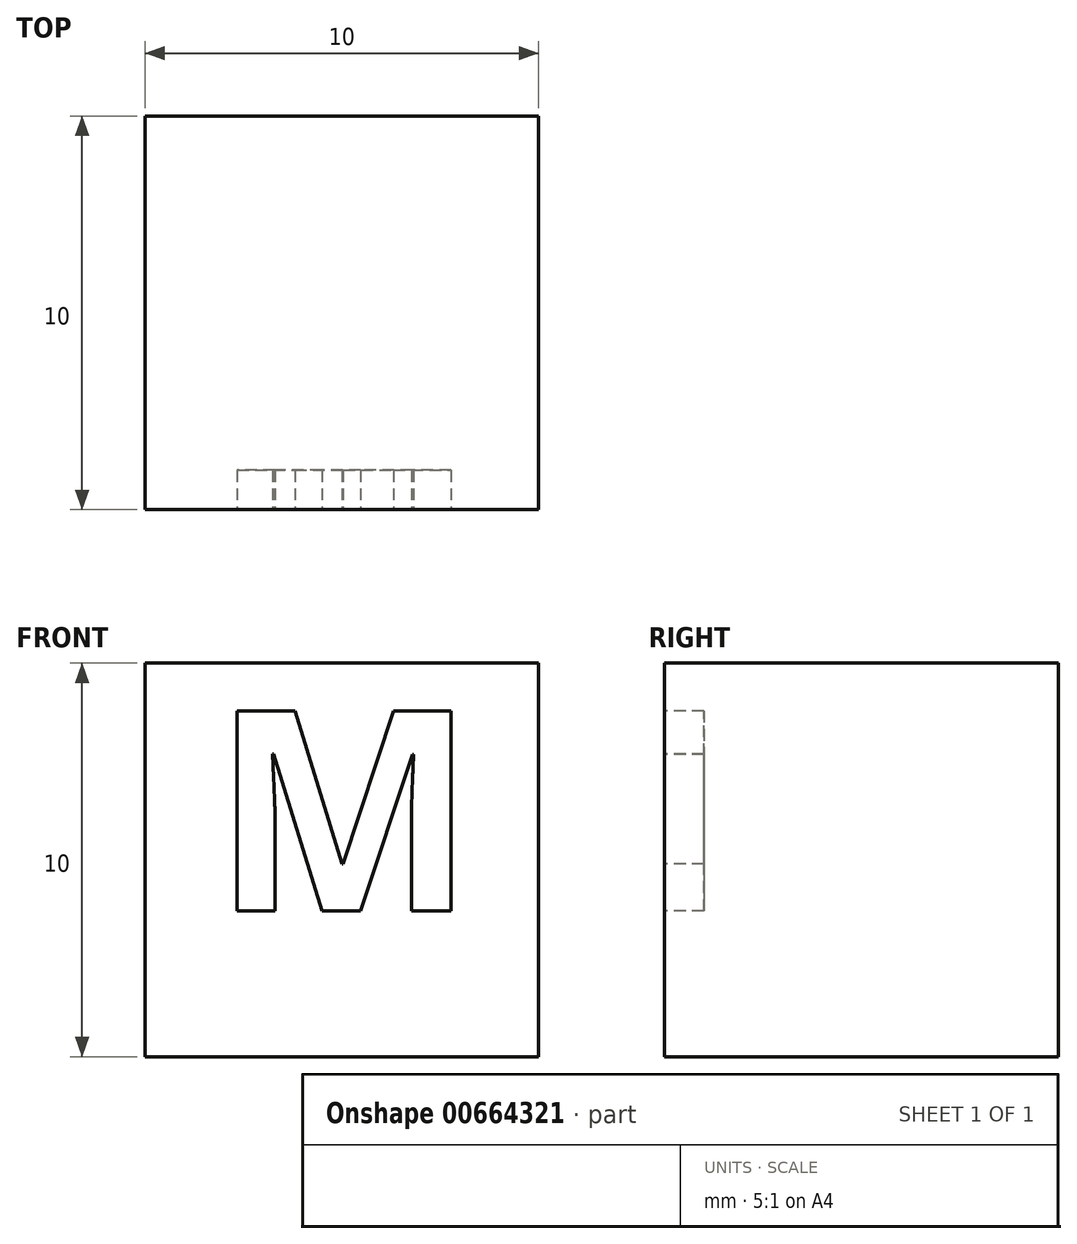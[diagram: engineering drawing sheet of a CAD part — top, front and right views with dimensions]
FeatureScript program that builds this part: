
annotation { "Feature Type Name" : "Feature", "Feature Type Description" : "" }
export const myFeature = defineFeature(function(context is Context, id is Id, definition is map)
    precondition{}
    {
        {
            var Q0;
            Q0=qCreatedBy(makeId("Top.planeOp"),FACE);
            var sketch = newSketch(context, id + "F0", { "sketchPlane" : qUnion([Q0])});
            skLineSegment(sketch, "E0.bottom", {"start": v(-5, 5) * mm, "end": v(5, 5) * mm});
            skLineSegment(sketch, "E0.top", {"start": v(-5, -5) * mm, "end": v(5, -5) * mm});
            skLineSegment(sketch, "E0.left", {"start": v(-5, 5) * mm, "end": v(-5, -5) * mm});
            skLineSegment(sketch, "E0.right", {"start": v(5, 5) * mm, "end": v(5, -5) * mm});
            skPoint(sketch, "E0.middle", {"position": v(0, 0) * mm});
            skSolve(sketch);
        }
        {
            var Q0;
            Q0 = qSketchRegion(id + "F0", true);
            extrude(context, id + "F1", {"entities" : qUnion([Q0]), "depth" : 10 * mm, "offsetDistance" : 25 * mm});
        }
        {
            var Q0;
            Q0=makeQuery(id+"F1.opExtrude","SWEPT_FACE",FACE,{"disambiguationData":[OSD([sQuery(id+"F0.wireOp",EDGE,"E0.top")])]});
            var sketch = newSketch(context, id + "F2", { "sketchPlane" : qUnion([Q0])});
            skText(sketch, "E1", { "text": "M\n", "fontName": "OpenSans-Bold.ttf"});
            const initialGuessF2  = {"E1": [-0.0033, 0.0037, 1, 0, 0.00513]};
            skSetInitialGuess(sketch, initialGuessF2);
            skSolve(sketch);
        }
        {
            var Q0;
            Q0 = qSketchRegion(id + "F2", true);
            extrude(context, id + "F3", {"entities" : qUnion([Q0]), "operationType" : NewBodyOperationType.REMOVE, "oppositeDirection" : true, "depth" : 1 * mm, "offsetDistance" : 25 * mm});
        }
    });
